# Revit family: WFR-CE
name_source: partatom
category: Specialty Equipment
units: mm (PartAtom-declared; Revit-internal decimal feet)

## family parameters
Cut with Voids When Loaded = No
Host = Face
Part Type = Normal
Room Calculation Point = No
Round Connector Dimension = Use Diameter
Shared = No

## types (60) — shared parameters
ABAA Compliance = Yes
Assembly Code = C3020200
CE Certification = 0679-CPR-1251
Default Elevation = 0"
Depth = 4"
Description = CE Marked, EN 1366-4 Tested Watertight Fire-resistant movement joint
Durometer Hardness of Silicone Coating (ASTM D2240) = Shore A: 25
European Technical Assessment = ETA-19/0222
Manufacturer = EMSEAL Joint Systems Ltd
Model = Emshield WFR-CE
Movement (of Nominal Material Size) = +50% / -50%
Product Data URL = https://bit.ly
Product Documentation URL = https://bit.ly
Product Page URL = https://cdn.emseal.com
Quint Bellow = No
R Value Range (ASTM C518) = 1.03 per 1-inch (25mm) depth
Rate of Air Leakage (ASTM E283) = Passed
Seal Material Note = Emshield WFR-CE is coated on the top and bottom with water-resistant silicone.
Staining (ASTM C510) = None
Temperature Range (ASTM C711) = 185°F (85°C) to -40°F (-40°C)
Tensile Strength (ASTM D3574) = 21 psi min; 145 kPa
Type Image = WFR-CE.png
URL = http://www.emseal.com

## per-type parameters (varying)
| type | Fire Resistence | Quad Bellow | Resistence to Fire EN 1366-4 | Single Bellow | Triple Bellow | Width |
| WFR - .5 inches - 1 hour | 1 HR | No | EI60 | Yes | No | 1/2" |
| WFR - .5 inches - 2 hour | 2 HR | No | EI120 | Yes | No | 1/2" |
| WFR - .5 inches - 3 hour | 3 HR | No | EI180 | Yes | No | 1/2" |
| WFR - .5 inches - 4 hour | 4 HR | No | EI240 | Yes | No | 1/2" |
| WFR - .75 inches - 1 hour | 1 HR | No | EI60 | Yes | No | 3/4" |
| WFR - .75 inches - 2 hour | 2 HR | No | EI120 | Yes | No | 3/4" |
| WFR - .75 inches - 3 hour | 3 HR | No | EI180 | Yes | No | 3/4" |
| WFR - .75 inches - 4 hour | 4 HR | No | EI240 | Yes | No | 3/4" |
| WFR - 1 inches - 1 hour | 1 HR | No | EI60 | Yes | No | 1" |
| WFR - 1 inches - 2 hour | 2 HR | No | EI120 | Yes | No | 1" |
| WFR - 1 inches - 3 hour | 3 HR | No | EI180 | Yes | No | 1" |
| WFR - 1 inches - 4 hour | 4 HR | No | EI240 | Yes | No | 1" |
| WFR - 1.25 inches - 1 hour | 1 HR | No | EI60 | Yes | No | 1 1/4" |
| WFR - 1.25 inches - 2 hour | 2 HR | No | EI120 | Yes | No | 1 1/4" |
| WFR - 1.25 inches - 3 hour | 3 HR | No | EI180 | Yes | No | 1 1/4" |
| WFR - 1.25 inches - 4 hour | 4 HR | No | EI240 | Yes | No | 1 1/4" |
| WFR - 1.5 inches - 1 hour | 1 HR | No | EI60 | No | Yes | 1 1/2" |
| WFR - 1.5 inches - 2 hour | 2 HR | No | EI120 | No | Yes | 1 1/2" |
| WFR - 1.5 inches - 3 hour | 3 HR | No | EI180 | No | Yes | 1 1/2" |
| WFR - 1.5 inches - 4 hour | 4 HR | No | EI240 | No | Yes | 1 1/2" |
| WFR - 1.75 inches - 1 hour | 1 HR | No | EI60 | No | Yes | 1 3/4" |
| WFR - 1.75 inches - 2 hour | 2 HR | No | EI120 | No | Yes | 1 3/4" |
| WFR - 1.75 inches - 3 hour | 3 HR | No | EI180 | No | Yes | 1 3/4" |
| WFR - 1.75 inches - 4 hour | 4 HR | No | EI240 | No | Yes | 1 3/4" |
| WFR - 2 inches - 1 hour | 1 HR | No | EI60 | No | Yes | 2" |
| WFR - 2 inches - 2 hour | 2 HR | No | EI120 | No | Yes | 2" |
| WFR - 2 inches - 3 hour | 3 HR | No | EI180 | No | Yes | 2" |
| WFR - 2 inches - 4 hour | 4 HR | No | EI240 | No | Yes | 2" |
| WFR - 2.25 inches - 1 hour | 1 HR | No | EI60 | No | Yes | 2 1/4" |
| WFR - 2.25 inches - 2 hour | 2 HR | No | EI120 | No | Yes | 2 1/4" |
| WFR - 2.25 inches - 3 hour | 3 HR | No | EI180 | No | Yes | 2 1/4" |
| WFR - 2.25 inches - 4 hour | 4 HR | No | EI240 | No | Yes | 2 1/4" |
| WFR - 2.5 inches - 1 hour | 1 HR | No | EI60 | No | Yes | 2 1/2" |
| WFR - 2.5 inches - 2 hour | 2 HR | No | EI120 | No | Yes | 2 1/2" |
| WFR - 2.5 inches - 3 hour | 3 HR | No | EI180 | No | Yes | 2 1/2" |
| WFR - 2.5 inches - 4 hour | 4 HR | No | EI240 | No | Yes | 2 1/2" |
| WFR - 2.75 inches - 1 hour | 1 HR | No | EI60 | No | Yes | 2 3/4" |
| WFR - 2.75 inches - 2 hour | 2 HR | No | EI120 | No | Yes | 2 3/4" |
| WFR - 2.75 inches - 3 hour | 3 HR | No | EI180 | No | Yes | 2 3/4" |
| WFR - 2.75 inches - 4 hour | 4 HR | No | EI240 | No | Yes | 2 3/4" |
| WFR - 3 inches - 1 hour | 1 HR | No | EI60 | No | Yes | 3" |
| WFR - 3 inches - 2 hour | 2 HR | No | EI120 | No | Yes | 3" |
| WFR - 3 inches - 3 hour | 3 HR | No | EI180 | No | Yes | 3" |
| WFR - 3 inches - 4 hour | 4 HR | No | EI240 | No | Yes | 3" |
| WFR - 3.25 inches - 1 hour | 1 HR | Yes | EI60 | No | No | 3 1/4" |
| WFR - 3.25 inches - 2 hour | 2 HR | Yes | EI120 | No | No | 3 1/4" |
| WFR - 3.25 inches - 3 hour | 3 HR | Yes | EI180 | No | No | 3 1/4" |
| WFR - 3.25 inches - 4 hour | 4 HR | Yes | EI240 | No | No | 3 1/4" |
| WFR - 3.5 inches - 1 hour | 1 HR | Yes | EI60 | No | No | 3 1/2" |
| WFR - 3.5 inches - 2 hour | 2 HR | Yes | EI120 | No | No | 3 1/2" |
| WFR - 3.5 inches - 3 hour | 3 HR | Yes | EI180 | No | No | 3 1/2" |
| WFR - 3.5 inches - 4 hour | 4 HR | Yes | EI240 | No | No | 3 1/2" |
| WFR - 3.75 inches - 1 hour | 1 HR | Yes | EI60 | No | No | 3 3/4" |
| WFR - 3.75 inches - 2 hour | 2 HR | Yes | EI120 | No | No | 3 3/4" |
| WFR - 3.75 inches - 3 hour | 3 HR | Yes | EI180 | No | No | 3 3/4" |
| WFR - 3.75 inches - 4 hour | 4 HR | Yes | EI240 | No | No | 3 3/4" |
| WFR - 4 inches - 1 hour | 1 HR | Yes | EI60 | No | No | 4" |
| WFR - 4 inches - 2 hour | 2 HR | Yes | EI120 | No | No | 4" |
| WFR - 4 inches - 3 hour | 3 HR | Yes | EI180 | No | No | 4" |
| WFR - 4 inches - 4 hour | 4 HR | Yes | EI240 | No | No | 4" |

## geometry (parser evidence)
native form markers: Sweep x2
no freeform markers — native parametric forms only
